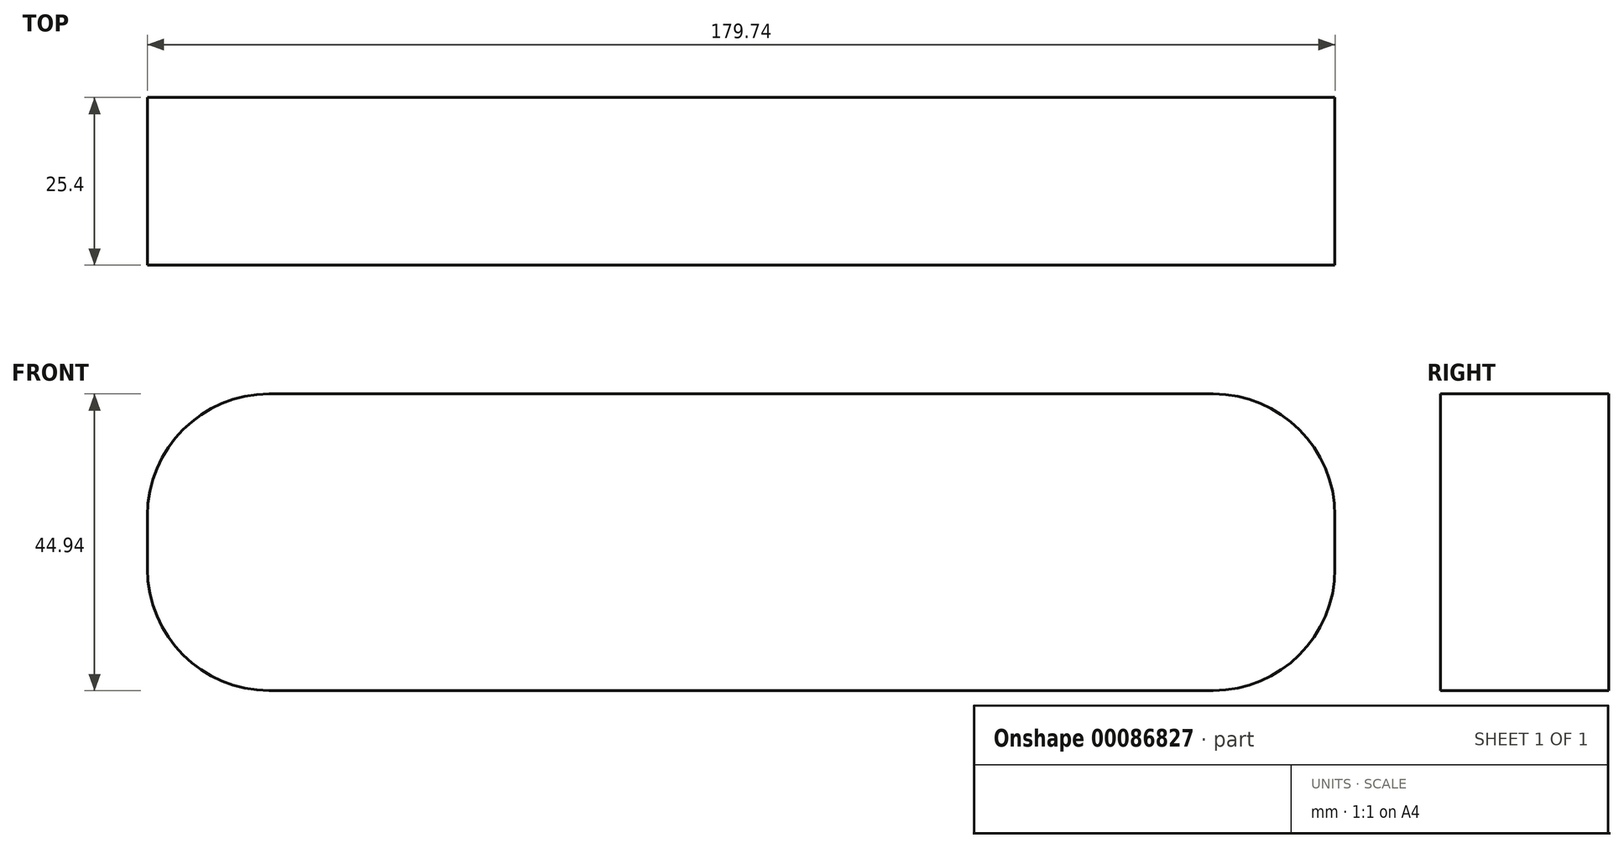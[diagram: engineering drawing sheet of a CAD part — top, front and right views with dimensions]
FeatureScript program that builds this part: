
annotation { "Feature Type Name" : "Feature", "Feature Type Description" : "" }
export const myFeature = defineFeature(function(context is Context, id is Id, definition is map)
    precondition{}
    {
        {
            var Q0;
            Q0=qCreatedBy(makeId("Front.planeOp"),FACE);
            var sketch = newSketch(context, id + "F0", { "sketchPlane" : qUnion([Q0])});
            skLineSegment(sketch, "E0.bottom", {"start": v(-71.42, 22.47) * mm, "end": v(71.42, 22.47) * mm});
            skLineSegment(sketch, "E0.top", {"start": v(-71.42, -22.47) * mm, "end": v(71.42, -22.47) * mm});
            skLineSegment(sketch, "E0.left", {"start": v(-89.87, 4.02) * mm, "end": v(-89.87, -4.02) * mm});
            skLineSegment(sketch, "E0.right", {"start": v(89.87, 4.02) * mm, "end": v(89.87, -4.02) * mm});
            skPoint(sketch, "E0.middle", {"position": v(0, 0) * mm});
            skPoint(sketch, "E1.visualSharp", {"position": v(-89.87, 22.47) * mm});
            skArc(sketch, "E1.filletArc", {"start": v(-71.42, 22.47) * mm, "mid": v(-84.46, 17.06) * mm, "end": v(-89.87, 4.02) * mm});
            skPoint(sketch, "E2.visualSharp", {"position": v(-89.87, -22.47) * mm});
            skArc(sketch, "E2.filletArc", {"start": v(-89.87, -4.02) * mm, "mid": v(-84.46, -17.06) * mm, "end": v(-71.42, -22.47) * mm});
            skPoint(sketch, "E3.visualSharp", {"position": v(89.87, 22.47) * mm});
            skArc(sketch, "E3.filletArc", {"start": v(89.87, 4.02) * mm, "mid": v(84.46, 17.06) * mm, "end": v(71.42, 22.47) * mm});
            skPoint(sketch, "E4.visualSharp", {"position": v(89.87, -22.47) * mm});
            skArc(sketch, "E4.filletArc", {"start": v(71.42, -22.47) * mm, "mid": v(84.46, -17.06) * mm, "end": v(89.87, -4.02) * mm});
            skSolve(sketch);
        }
        {
            var Q0;
            Q0 = qSketchRegion(id + "F0", true);
            extrude(context, id + "F1", {"entities" : qUnion([Q0]), "depth" : 25.4 * mm});
        }
    });
